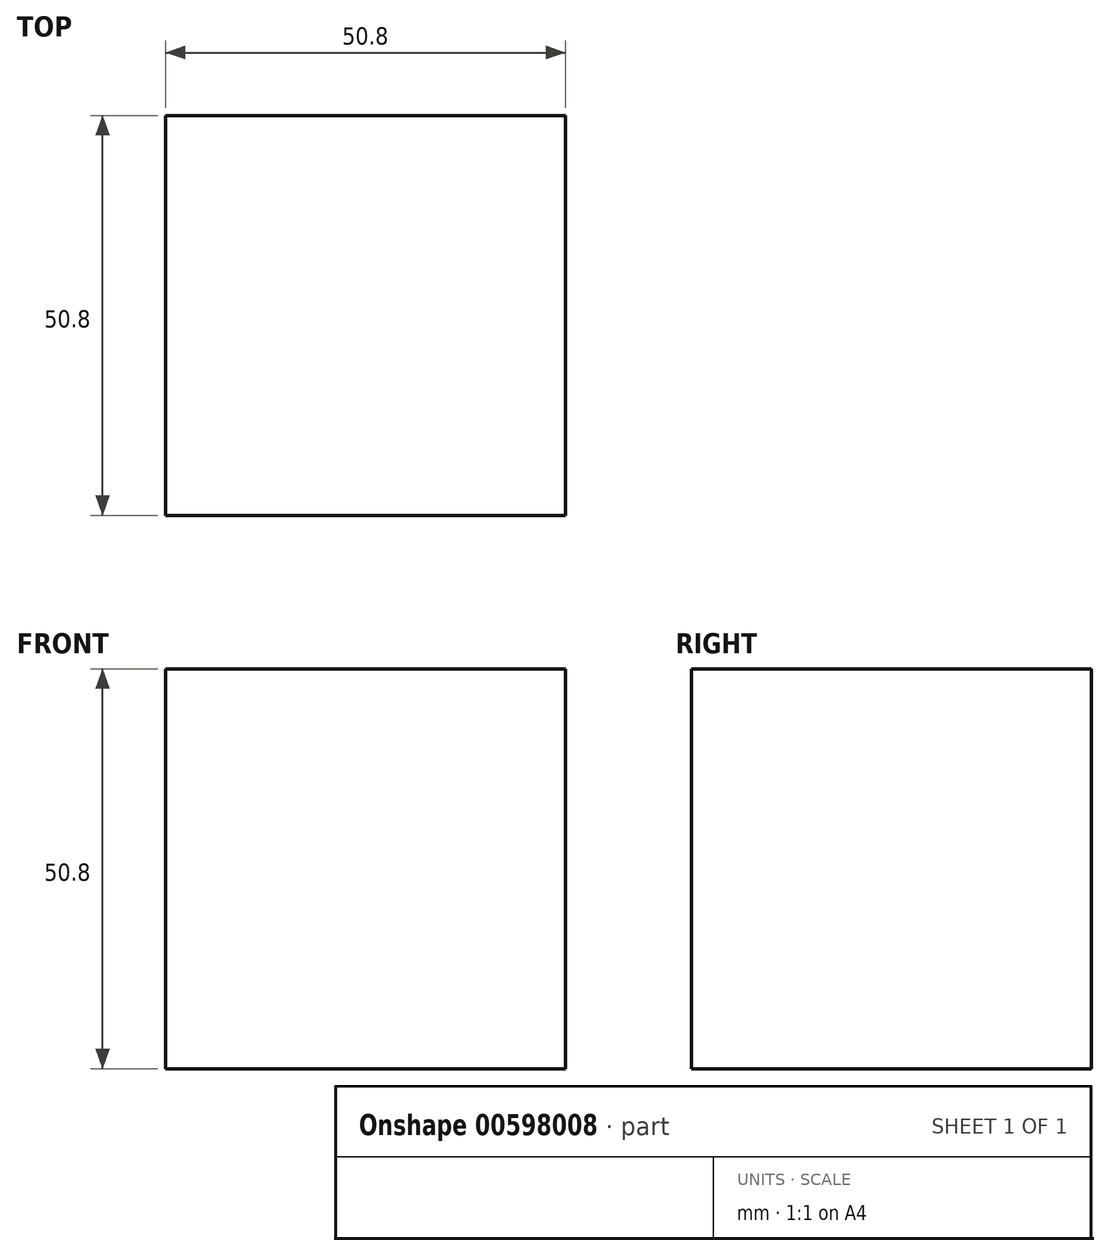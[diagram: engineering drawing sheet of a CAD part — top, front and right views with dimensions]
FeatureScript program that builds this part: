
annotation { "Feature Type Name" : "Feature", "Feature Type Description" : "" }
export const myFeature = defineFeature(function(context is Context, id is Id, definition is map)
    precondition{}
    {
        {
            var Q0;
            Q0=qCreatedBy(makeId("Top.planeOp"),FACE);
            var sketch = newSketch(context, id + "F0", { "sketchPlane" : qUnion([Q0])});
            skLineSegment(sketch, "E0", {"start": v(-40.59, 16.56) * mm, "end": v(-40.59, -34.24) * mm});
            skLineSegment(sketch, "E1", {"start": v(-40.59, -34.24) * mm, "end": v(10.21, -34.24) * mm});
            skLineSegment(sketch, "E2", {"start": v(10.21, -34.24) * mm, "end": v(10.21, 16.56) * mm});
            skLineSegment(sketch, "E3", {"start": v(-40.59, 16.56) * mm, "end": v(10.21, 16.56) * mm});
            skSolve(sketch);
        }
        {
            var Q0;
            Q0=makeQuery(id+"F0.imprint","IMPRINT",FACE,{"disambiguationData":[TD([[makeQuery(id+"F0.imprint","IMPRINT",EDGE,{"derivedFrom":sQuery(id+"F0.wireOp",EDGE,"E0")}),1.0]])]});
            extrude(context, id + "F1", {"entities" : qUnion([Q0]), "depth" : 50.8 * mm, "offsetDistance" : 25.4 * mm});
        }
    });
